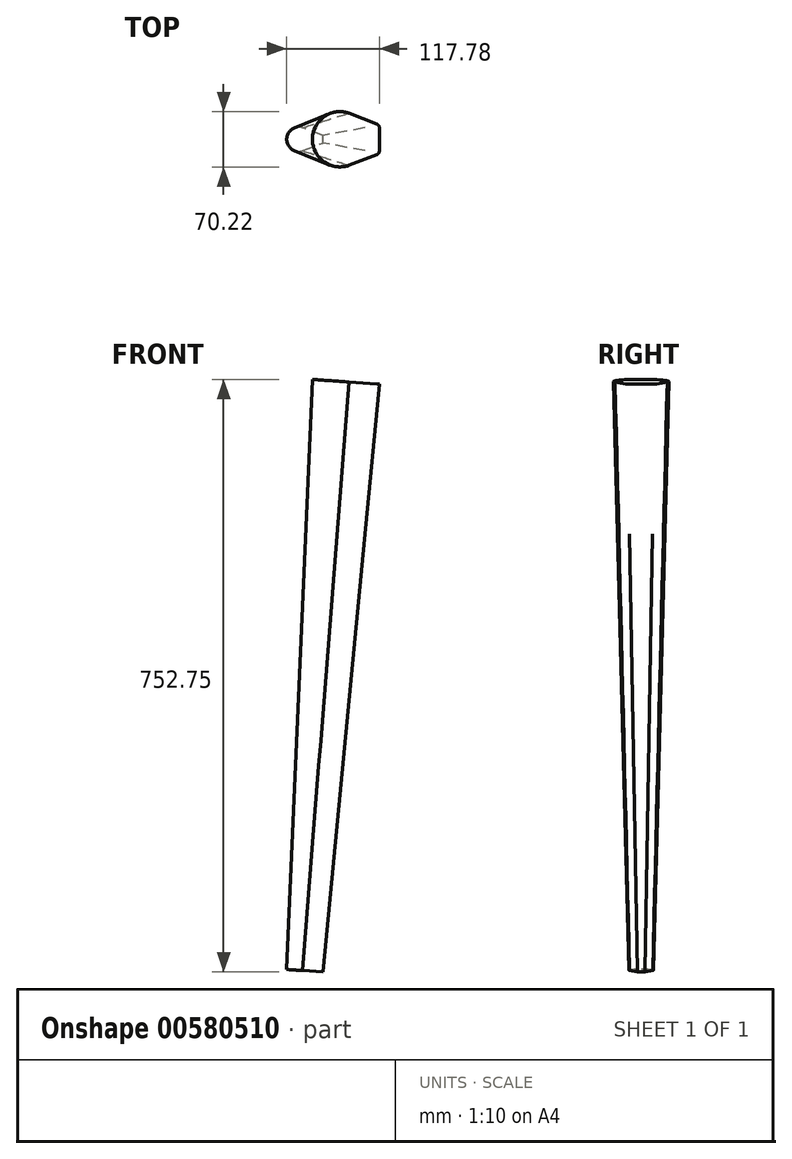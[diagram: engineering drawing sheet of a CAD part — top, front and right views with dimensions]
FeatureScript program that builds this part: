
annotation { "Feature Type Name" : "Feature", "Feature Type Description" : "" }
export const myFeature = defineFeature(function(context is Context, id is Id, definition is map)
    precondition{}
    {
        {
            var Q0;
            Q0=qCreatedBy(makeId("Top.planeOp"),FACE);
            var sketch = newSketch(context, id + "F0", { "sketchPlane" : qUnion([Q0])});
            skArc(sketch, "E0", {"start": v(11.58, 33.14) * mm, "mid": v(-35.1, 0) * mm, "end": v(11.58, -33.14) * mm});
            skLineSegment(sketch, "E1", {"start": v(50.15, 0) * mm, "end": v(50.15, 14.63) * mm});
            skLineSegment(sketch, "E2", {"start": v(50.15, 0) * mm, "end": v(50.15, -14.63) * mm});
            skLineSegment(sketch, "E3", {"start": v(46.97, 19.3) * mm, "end": v(11.58, 33.14) * mm});
            skLineSegment(sketch, "E4", {"start": v(11.58, -33.14) * mm, "end": v(46.97, -19.3) * mm});
            skArc(sketch, "E5.filletArc", {"start": v(50.15, 14.63) * mm, "mid": v(49.28, 17.46) * mm, "end": v(46.97, 19.3) * mm});
            skArc(sketch, "E6.filletArc", {"start": v(46.97, -19.3) * mm, "mid": v(49.28, -17.46) * mm, "end": v(50.15, -14.63) * mm});
            skSolve(sketch);
        }
        {
            var Q0;
            Q0 = qSketchRegion(id + "F0", true);
            extrude(context, id + "F1", {"entities" : qUnion([Q0]), "oppositeDirection" : true, "depth" : 750 * mm, "offsetDistance" : 25 * mm, "hasDraft" : true, "draftAngle" : 1.5 * degree, "draftPullDirection" : true});
        }
        {
            var Q0;
            Q0=makeQuery(id+"F1.opExtrude","SWEPT_BODY",BODY,{"disambiguationData":[OSD([sQuery(id+"F0.wireOp",EDGE,"E0"),sQuery(id+"F0.wireOp",EDGE,"E1"),sQuery(id+"F0.wireOp",EDGE,"E2"),sQuery(id+"F0.wireOp",EDGE,"E3"),sQuery(id+"F0.wireOp",EDGE,"E4"),sQuery(id+"F0.wireOp",EDGE,"E5.filletArc"),sQuery(id+"F0.wireOp",EDGE,"E6.filletArc")])]});
            var Q1;
            Q1=makeQuery(id+"F1.opExtrude","CAP_EDGE",EDGE,{"disambiguationData":[OSD([sQuery(id+"F0.wireOp",EDGE,"E1"),sQuery(id+"F0.wireOp",EDGE,"E2")])],"isStart":true});
            transform(context, id + "F2", {"entities" : qUnion([Q0]), "transformType" : TransformType.ROTATION, "transformAxis" : qUnion([Q1]), "angle" : 4 * degree, "makeCopy" : false});
        }
    });
